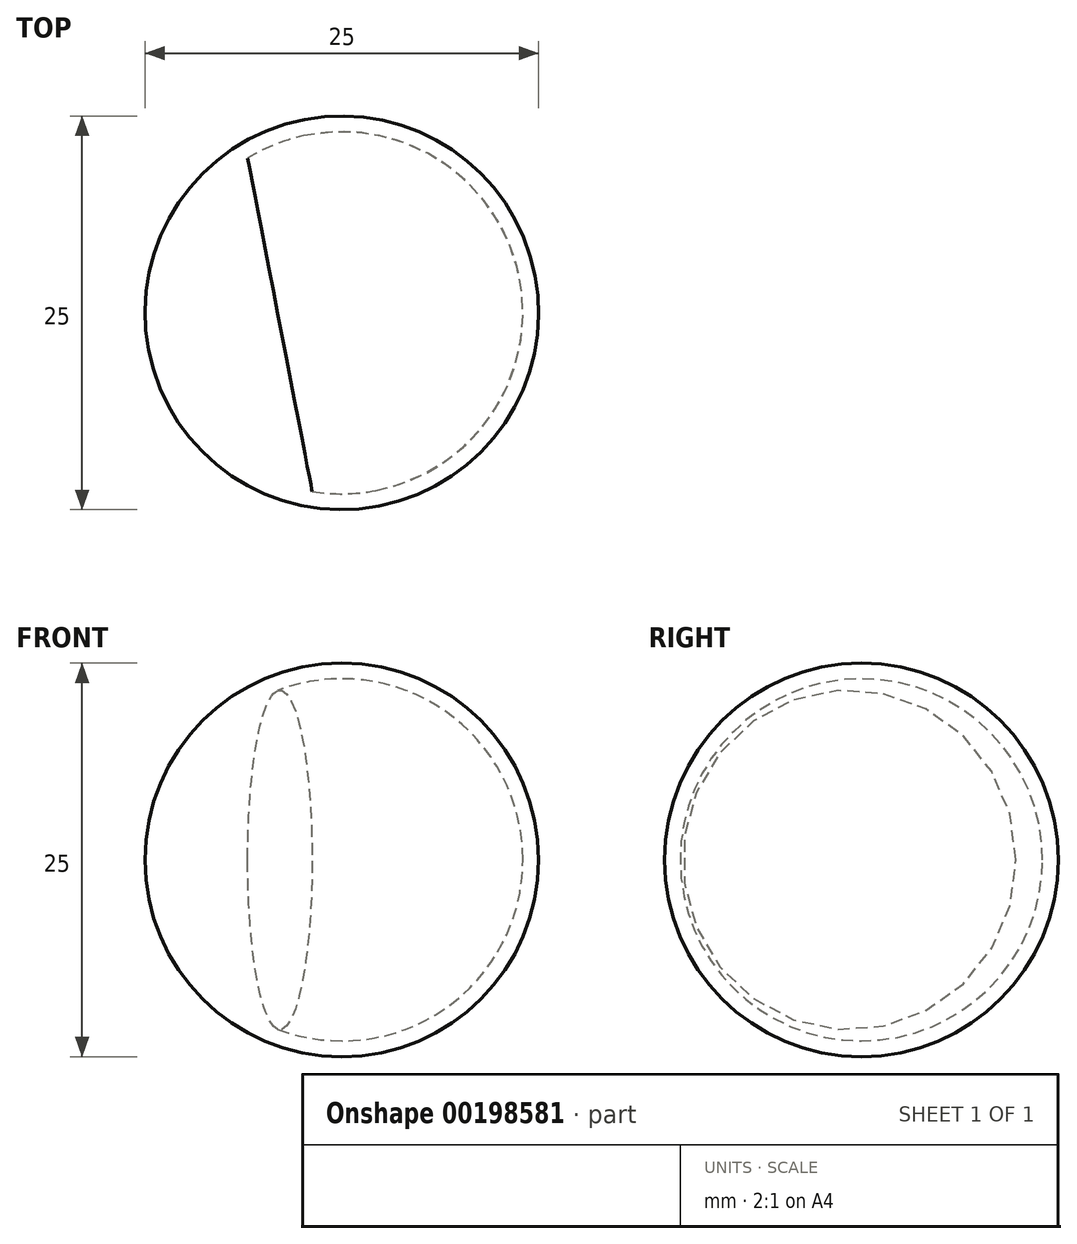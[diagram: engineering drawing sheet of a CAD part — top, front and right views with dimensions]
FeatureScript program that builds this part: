
annotation { "Feature Type Name" : "Feature", "Feature Type Description" : "" }
export const myFeature = defineFeature(function(context is Context, id is Id, definition is map)
    precondition{}
    {
        {
            var Q0;
            Q0=qCreatedBy(makeId("Top.planeOp"),FACE);
            var sketch = newSketch(context, id + "F0", { "sketchPlane" : qUnion([Q0])});
            skCircle(sketch, "E0", {"center": v(0, 0) * mm, "radius": 12.5 * mm});
            skLineSegment(sketch, "E1", {"start": v(-2.37, 12.27) * mm, "end": v(0, 0) * mm});
            skLineSegment(sketch, "E2", {"start": v(-2.37, 12.27) * mm, "end": v(2.37, -12.27) * mm});
            skLineSegment(sketch, "E3", {"start": v(-6.18, 10.87) * mm, "end": v(-1.68, -12.39) * mm});
            skSolve(sketch);
        }
        {
            var Q0;
            {var subQ0=sQuery(id+"F0.wireOp",EDGE,"E3");Q0=makeQuery(id+"F0.imprint","IMPRINT",FACE,{"disambiguationData":[TD([[makeQuery(id+"F0.imprint","IMPRINT",EDGE,{"derivedFrom":subQ0}),-1.0]])]});}
            var Q1;
            {var subQ5=sQuery(id+"F0.wireOp",EDGE,"E3");Q1=makeQuery(id+"F0.imprint","IMPRINT",FACE,{"disambiguationData":[TD([[makeQuery(id+"F0.imprint","IMPRINT",EDGE,{"derivedFrom":subQ5}),1.0]])]});}
            var Q2;
            Q2=sQuery(id+"F0.wireOp",EDGE,"E2");
            revolve(context, id + "F1", {"entities" : qUnion([Q0, Q1]), "axis" : qUnion([Q2]), "revolveType" : RevolveType.FULL});
        }
        {
            var Q0;
            Q0=makeQuery(id+"F1.opRevolve","SWEPT_FACE",FACE,{"disambiguationData":[OSD([sQuery(id+"F0.wireOp",EDGE,"E0")])]});
            var Q1;
            Q1=makeQuery(id+"F1.opRevolve","SWEPT_BODY",BODY,{"disambiguationData":[OSD([sQuery(id+"F0.wireOp",EDGE,"E0"),sQuery(id+"F0.wireOp",EDGE,"E2")])]});
            shell(context, id + "F2", {"isHollow" : true, "entities" : qUnion([Q0]), "parts" : qUnion([Q1]), "thickness" : 1 * mm});
        }
        {
            var Q0;
            {var subQ0=sQuery(id+"F0.wireOp",EDGE,"E3");Q0=makeQuery(id+"F0.imprint","IMPRINT",FACE,{"disambiguationData":[TD([[makeQuery(id+"F0.imprint","IMPRINT",EDGE,{"derivedFrom":subQ0}),-1.0]])]});}
            extrude(context, id + "F3", {"entities" : qUnion([Q0]), "operationType" : NewBodyOperationType.ADD, "endBound" : BoundingType.UP_TO_NEXT, "depth" : 25 * mm, "hasSecondDirection" : true, "secondDirectionOppositeDirection" : true, "secondDirectionDepth" : 25 * mm});
        }
    });
